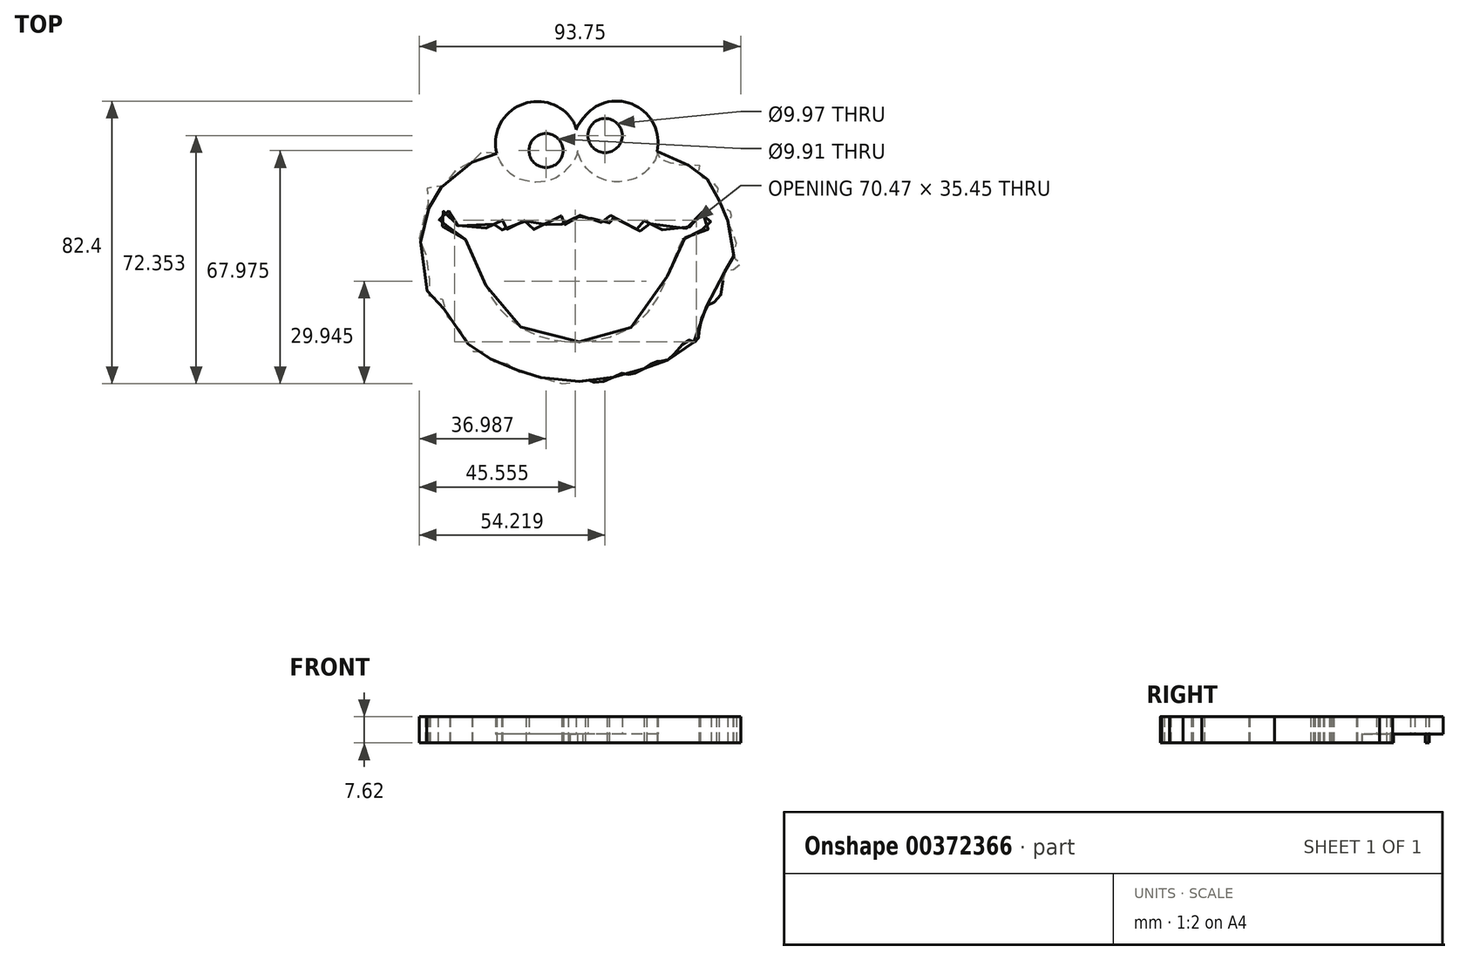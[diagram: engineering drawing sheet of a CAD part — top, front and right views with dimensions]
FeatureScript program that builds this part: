
annotation { "Feature Type Name" : "Feature", "Feature Type Description" : "" }
export const myFeature = defineFeature(function(context is Context, id is Id, definition is map)
    precondition{}
    {
        {
            var Q0;
            Q0=qCreatedBy(makeId("Top.planeOp"),FACE);
            var sketch = newSketch(context, id + "F0", { "sketchPlane" : qUnion([Q0])});
            skArc(sketch, "E0", {"start": v(-3.13, 41.43) * mm, "mid": v(-17.96, 43.84) * mm, "end": v(-24.03, 30.1) * mm});
            skArc(sketch, "E1", {"start": v(22.72, 30.8) * mm, "mid": v(16.34, 44.17) * mm, "end": v(1.82, 41.25) * mm});
            skCircle(sketch, "E2", {"center": v(-9.65, 31.01) * mm, "radius": 4.96 * mm});
            skPoint(sketch, "E2.first.point", {"position": v(-5.61, 28.15) * mm});
            skPoint(sketch, "E2.second.point", {"position": v(-13.61, 34) * mm});
            skPoint(sketch, "E2.third.point", {"position": v(-6.5, 34.84) * mm});
            skCircle(sketch, "E3", {"center": v(7.58, 35.4) * mm, "radius": 4.99 * mm});
            skPoint(sketch, "E3.first.point", {"position": v(4.87, 39.58) * mm});
            skPoint(sketch, "E3.second.point", {"position": v(10.3, 31.2) * mm});
            skPoint(sketch, "E3.third.point", {"position": v(12.4, 34.1) * mm});
            skFitSpline(sketch, "E4", {"points": [v(-24.03, 30.1) * mm, v(-25.35, 28.94) * mm, v(-29.35, 30.68) * mm, v(-31.2, 29.1) * mm, v(-31.2, 27.58) * mm, v(-34.46, 25.84) * mm, v(-38.25, 23.52) * mm, v(-39.88, 20.42) * mm, v(-43.32, 20.4) * mm, v(-44.6, 19.64) * mm, v(-44.6, 17.47) * mm, v(-43.76, 14.38) * mm, v(-44.07, 13.45) * mm, v(-45.75, 10.35) * mm, v(-46.64, 5.66) * mm, v(-46.37, 4.81) * mm, v(-44.51, 0.39) * mm, v(-43.5, -5.54) * mm, v(-44.42, -10.41) * mm, v(-44.16, -11.17) * mm, v(-41.5, -10.9) * mm, v(-40, -11.96) * mm, v(-39.42, -14.7) * mm, v(-38.1, -17.76) * mm, v(-35.4, -20.48) * mm, v(-34.73, -21.45) * mm, v(-30.67, -27.67) * mm, v(-30.04, -27.89) * mm, v(-29.22, -27.6) * mm, v(-28.55, -27.4) * mm, v(-27.59, -28) * mm, v(-25.28, -30.09) * mm, v(-22.63, -30.9) * mm, v(-21.78, -30.94) * mm, v(-20.66, -31.17) * mm, v(-19.28, -32.06) * mm, v(-16.72, -33.88) * mm, v(-15.04, -34.44) * mm, v(-13.85, -34.37) * mm, v(-13.3, -34.18) * mm, v(-12.58, -34.48) * mm, v(-11.06, -35.15) * mm, v(-6.03, -36.64) * mm, v(-4.17, -36.94) * mm, v(-1.97, -36.79) * mm, v(2.5, -35.86) * mm, v(3.39, -36.27) * mm, v(5.28, -36.49) * mm, v(8.78, -35.74) * mm, v(11.87, -34.07) * mm, v(13.62, -33.96) * mm, v(15.05, -34.3) * mm, v(16.9, -33.55) * mm, v(19.83, -31.95) * mm, v(21.47, -30.9) * mm, v(22.88, -30.32) * mm, v(23.68, -30.23) * mm, v(24.83, -30.36) * mm, v(26.12, -29.74) * mm, v(28.15, -27.8) * mm, v(31.47, -24.3) * mm, v(32.67, -24.34) * mm, v(33.6, -24.83) * mm, v(34.48, -24.3) * mm, v(34.88, -22.79) * mm, v(35.06, -20.93) * mm, v(37.45, -13.98) * mm, v(39.17, -13.27) * mm, v(41.34, -11.01) * mm, v(42.32, -4.68) * mm, v(43.47, -3.58) * mm, v(45.64, -3.49) * mm, v(47.1, -1.67) * mm, v(46.04, -1) * mm, v(44.97, 0.94) * mm, v(45.74, 3.03) * mm, v(45.48, 5.82) * mm, v(43.37, 9.97) * mm, v(43.74, 11.45) * mm, v(44.9, 12.34) * mm, v(43.9, 13.4) * mm, v(42.43, 14.03) * mm, v(40.69, 16.82) * mm, v(40.1, 18.19) * mm, v(40.58, 18.6) * mm, v(40.74, 19.56) * mm, v(40.1, 20.71) * mm, v(37.69, 22.6) * mm, v(35.32, 23.5) * mm, v(34.95, 24.93) * mm, v(35.27, 26.56) * mm, v(33.2, 26.94) * mm, v(30.76, 26.63) * mm, v(26.94, 27.32) * mm, v(23.5, 28.57) * mm, v(22.72, 30.8) * mm], "startDerivative": vector(-111.47, -191.66) * mm, "endDerivative": vector(-30.28, 232.63) * mm});
            skFitSpline(sketch, "E5", {"points": [v(-3.13, 41.43) * mm, v(-1.5, 39.09) * mm, v(-0.6, 36.09) * mm, v(-0.5, 32.3) * mm, v(-1.18, 28.98) * mm, v(-2.23, 27.19) * mm, v(-4.55, 24.82) * mm, v(-7.97, 22.82) * mm, v(-12.07, 22.03) * mm, v(-16.34, 22.66) * mm, v(-20.13, 24.82) * mm, v(-23.02, 28.19) * mm, v(-24.03, 30.1) * mm], "startDerivative": vector(23.82, -29.39) * mm, "endDerivative": vector(-12.35, 26.88) * mm});
            skFitSpline(sketch, "E6", {"points": [v(1.82, 41.25) * mm, v(-0.24, 38.46) * mm, v(-0.6, 37.78) * mm, v(-0.8, 37.19) * mm], "startDerivative": vector(-4.76, -6.2) * mm, "endDerivative": vector(-0.95, -2.72) * mm});
            skFitSpline(sketch, "E7", {"points": [v(22.83, 29.96) * mm, v(21.82, 27.88) * mm, v(20.41, 26.03) * mm, v(18.1, 24) * mm, v(15.37, 22.71) * mm, v(11.43, 22.09) * mm, v(7.86, 22.53) * mm, v(4.5, 24.06) * mm, v(2.2, 26) * mm, v(0.72, 28.07) * mm, v(-0.28, 30.38) * mm, v(-0.59, 31.44) * mm], "startDerivative": vector(-11.29, -25.92) * mm, "endDerivative": vector(-4.33, 16.56) * mm});
            skFitSpline(sketch, "E8", {"points": [v(-33.18, 5.16) * mm, v(-30.13, -1.42) * mm, v(-28.23, -5.63) * mm, v(-26.13, -10.58) * mm, v(-23.18, -15.11) * mm, v(-16.65, -20.64) * mm, v(-8.44, -24) * mm, v(-0.75, -24.74) * mm, v(5.46, -24.17) * mm, v(11.83, -22.22) * mm, v(18.36, -17.9) * mm, v(24, -9.98) * mm, v(26.82, -2.53) * mm, v(29.06, 2.53) * mm, v(29.62, 4.4) * mm, v(31.47, 5.87) * mm, v(33.53, 6.6) * mm, v(35.32, 7.66) * mm, v(35.97, 8) * mm, v(37, 8.06) * mm, v(37.44, 7.97) * mm, v(37.76, 8.1) * mm, v(38.35, 8.97) * mm, v(38.35, 10.44) * mm, v(37.79, 11.98) * mm, v(37.08, 12.8) * mm, v(36.28, 13.12) * mm, v(35.8, 12.94) * mm, v(35.4, 12.05) * mm, v(34.82, 10.6) * mm, v(34.37, 9.8) * mm, v(33.49, 9.31) * mm, v(31.36, 8.38) * mm, v(28.44, 7.8) * mm, v(24.95, 7.76) * mm, v(21.14, 9.18) * mm, v(20.34, 9.97) * mm, v(19.85, 10.2) * mm, v(19.01, 10.6) * mm, v(19.15, 9.8) * mm, v(19.54, 6.88) * mm, v(17.86, 7.54) * mm, v(15.78, 8.38) * mm, v(13.3, 9.62) * mm, v(10.7, 11.17) * mm, v(9.14, 12.1) * mm, v(8.48, 12.5) * mm, v(8.17, 12.19) * mm, v(8.39, 11.61) * mm, v(8.83, 9.89) * mm, v(8.48, 9.53) * mm, v(7.46, 9.75) * mm, v(5.32, 10.43) * mm, v(3.57, 11.23) * mm, v(2.38, 12.2) * mm, v(1.85, 12.63) * mm, v(1.12, 12.76) * mm, v(0.43, 12.27) * mm, v(-0.52, 11.45) * mm, v(-1.23, 10.92) * mm, v(-2.3, 10.3) * mm, v(-3, 9.8) * mm, v(-4.09, 9.44) * mm, v(-5.02, 9.53) * mm, v(-5.02, 9.88) * mm, v(-4.84, 10.55) * mm, v(-4.55, 12.25) * mm, v(-5.1, 12.07) * mm, v(-5.97, 11.74) * mm, v(-10.64, 8.82) * mm, v(-13.8, 7.98) * mm, v(-15.12, 8.23) * mm, v(-15.4, 9.1) * mm, v(-15.43, 9.8) * mm, v(-15.56, 10.42) * mm, v(-16.72, 10.55) * mm, v(-17.9, 9.67) * mm, v(-19.35, 8.73) * mm, v(-20.85, 8.1) * mm, v(-22.41, 7.89) * mm, v(-22.6, 8.23) * mm, v(-22.29, 8.92) * mm, v(-22.42, 9.63) * mm, v(-22.3, 10.74) * mm, v(-22.96, 10.56) * mm, v(-24.19, 10.22) * mm, v(-24.97, 9.44) * mm, v(-27.07, 8.5) * mm, v(-29.55, 7.95) * mm, v(-33.35, 8.29) * mm, v(-36.6, 10) * mm, v(-37.54, 11.06) * mm, v(-37.6, 11.79) * mm, v(-37.57, 12.79) * mm, v(-38.5, 13.5) * mm, v(-39.56, 13.39) * mm, v(-39.88, 12.91) * mm, v(-40.28, 12) * mm, v(-40.7, 11.11) * mm, v(-40.86, 10.48) * mm, v(-41.1, 9.72) * mm, v(-40.3, 9.25) * mm, v(-39.86, 9) * mm, v(-38.83, 9.04) * mm, v(-37.54, 8.27) * mm, v(-35.62, 6.9) * mm, v(-33.99, 5.77) * mm, v(-33.18, 5.16) * mm]});
            skSolve(sketch);
        }
        {
            var Q0;
            Q0=makeQuery(id+"F0.imprint","IMPRINT",FACE,{"disambiguationData":[TD([[makeQuery(id+"F0.imprint","IMPRINT",EDGE,{"derivedFrom":sQuery(id+"F0.wireOp",EDGE,"E1")}),1.0]])]});
            var Q1;
            {var subQ3=sQuery(id+"F0.wireOp",EDGE,"E0");Q1=makeQuery(id+"F0.imprint","IMPRINT",FACE,{"disambiguationData":[TD([[makeQuery(id+"F0.imprint","IMPRINT",EDGE,{"derivedFrom":subQ3}),1.0]])]});}
            extrude(context, id + "F1", {"entities" : qUnion([Q0, Q1]), "depth" : 7.62 * mm});
        }
        {
            var Q0;
            Q0=qCreatedBy(makeId("Top.planeOp"),FACE);
            var sketch = newSketch(context, id + "F2", { "sketchPlane" : qUnion([Q0])});
            skArc(sketch, "E9.0", {"start": v(-3.13, 41.43) * mm, "mid": v(-17.96, 43.84) * mm, "end": v(-24.03, 30.1) * mm});
            skFitSpline(sketch, "E10.0", {"points": [v(-3.13, 41.43) * mm, v(-2.53, 40.68) * mm, v(-1.3, 39.16) * mm, v(-0.46, 36.06) * mm, v(-0.34, 32.36) * mm, v(-1.03, 28.92) * mm, v(-2.18, 27.14) * mm, v(-4.5, 24.62) * mm, v(-7.9, 22.59) * mm, v(-12.07, 21.8) * mm, v(-16.45, 22.42) * mm, v(-20.25, 24.52) * mm, v(-23.1, 28.07) * mm, v(-23.76, 29.5) * mm, v(-24.03, 30.1) * mm]});
            skFitSpline(sketch, "E11.0", {"points": [v(22.83, 29.96) * mm, v(22.52, 29.25) * mm, v(21.89, 27.8) * mm, v(20.46, 25.98) * mm, v(18.13, 23.83) * mm, v(15.42, 22.56) * mm, v(11.4, 21.9) * mm, v(7.85, 22.33) * mm, v(4.45, 23.91) * mm, v(2.12, 25.92) * mm, v(0.67, 27.94) * mm, v(-0.3, 30.33) * mm, v(-0.5, 31.13) * mm, v(-0.59, 31.44) * mm]});
            skArc(sketch, "E12.0", {"start": v(22.72, 30.8) * mm, "mid": v(16.34, 44.17) * mm, "end": v(1.82, 41.25) * mm});
            skFitSpline(sketch, "E13.0", {"points": [v(1.82, 41.25) * mm, v(0.99, 40.16) * mm, v(-0.24, 38.56) * mm, v(-0.6, 37.82) * mm, v(-0.74, 37.4) * mm, v(-0.8, 37.19) * mm]});
            skLineSegment(sketch, "E14", {"start": v(22.83, 29.96) * mm, "end": v(22.72, 30.8) * mm});
            skFitSpline(sketch, "E15.trimOffspring", {"points": [v(-3.13, 41.43) * mm, v(-2.53, 40.68) * mm, v(-1.3, 39.16) * mm, v(-0.46, 36.06) * mm, v(-0.34, 32.36) * mm, v(-1.03, 28.92) * mm, v(-2.18, 27.14) * mm, v(-4.5, 24.62) * mm, v(-7.9, 22.59) * mm, v(-12.07, 21.8) * mm, v(-16.45, 22.42) * mm, v(-20.25, 24.52) * mm, v(-23.1, 28.07) * mm, v(-23.76, 29.5) * mm, v(-24.03, 30.1) * mm]});
            skSolve(sketch);
        }
        {
            var Q0;
            Q0 = qSketchRegion(id + "F2", true);
            extrude(context, id + "F3", {"entities" : qUnion([Q0]), "operationType" : NewBodyOperationType.REMOVE, "depth" : 2.54 * mm});
        }
    });
